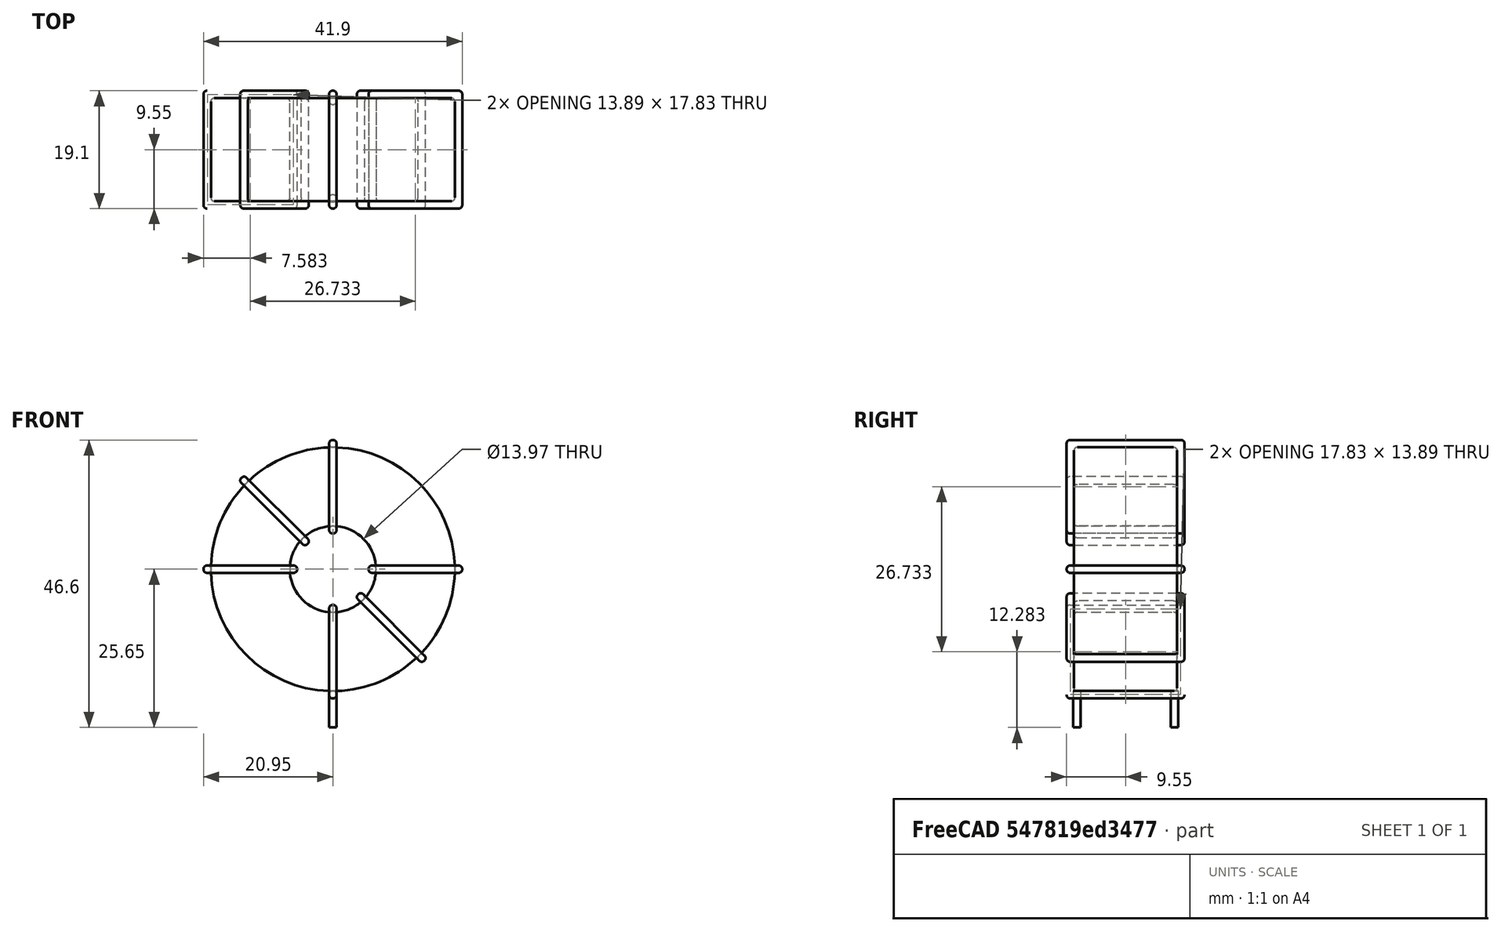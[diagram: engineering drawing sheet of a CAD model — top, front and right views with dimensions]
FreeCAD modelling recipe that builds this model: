
FCSTD DOCUMENT  (FreeCAD 0.16R6703 (Git))
Label: L_Toroid_Vertical_L41.9mm_W19.1mm_P15.80mm_Vishay_TJ7
License: All rights reserved
LicenseURL: http://en.wikipedia.org/wiki/All_rights_reserved
objects: Sketcher::SketchObject×6, PartDesign::Pad×6, PartDesign::Fillet×5, Spreadsheet::Sheet×1
note: 23 computed .brp shape members not serialized (recipe doc carries the construction recipe); baked Part::Feature solids carry a one-line shape summary decoded from their .brp

FEATURE [Spreadsheet::Sheet] Spreadsheet  label="dimensions"
  cells = A1=Wx; B1(Wx)=41.9; C1(WW)=13.96666666666667; D1=41.9; A2=Wy; B2(Wy)=19.1; D2=19.1; A3=RM; B3(RMx)=15.8; C3(RMy)=0; A4=d_wire; B4(d_wire)=1.2; A5=H; B5(H)=41.9; A6=offsetx; B6(offsetx)=20.95
FEATURE [Sketcher::SketchObject] Sketch
  Placement = pos=(0,-7.9,0) rot=(1,0,0;1.5708rad)
  expr: Placement.Base.y = -Spreadsheet.RMx / 2
  expr: Constraints[0] = Spreadsheet.Wx / 2 - Spreadsheet.d_wire
  expr: Constraints[4] = Spreadsheet.WW / 2
  expr: Constraints[2] = Spreadsheet.Wx / 2 + Spreadsheet.d_wire + 0.5
  sketch-geometry (2):
    g0: Circle CenterX=0 CenterY=22.65 CenterZ=0 NormalX=0 NormalY=0 NormalZ=1 Radius=19.75
    g1: Circle CenterX=0 CenterY=22.65 CenterZ=0 NormalX=0 NormalY=0 NormalZ=1 Radius=6.98333
  constraints (5):
    c: Radius(g0) = 19.75
    c: DistanceX(g-1,g0) = 0
    c: DistanceY(g-1,g0) = 22.65
    c: Coincident(g1,g0)
    c: Radius(g1) = 6.98333
FEATURE [PartDesign::Pad] Pad
  Length = 16.7
  Length2 = 100
  Midplane = true
  Placement = pos=(0,-7.9,0) rot=(1,0,0;1.5708rad)
  Sketch = -> Sketch
  Type = 0
  expr: Length = Spreadsheet.Wy - 2 * Spreadsheet.d_wire
FEATURE [Sketcher::SketchObject] Sketch001
  Placement = pos=(0,0,1.7) rot=(0,0,1;0rad)
  expr: Placement.Base.z = 0.5 + Spreadsheet.d_wire
  expr: Constraints[4] = Spreadsheet.RMy
  expr: Constraints[2] = -Spreadsheet.RMx
  expr: Constraints[1] = Spreadsheet.d_wire / 2
  sketch-geometry (2):
    g0: Circle CenterX=0 CenterY=0 CenterZ=0 NormalX=0 NormalY=0 NormalZ=1 Radius=0.6
    g1: Circle CenterX=0 CenterY=-15.8 CenterZ=0 NormalX=0 NormalY=0 NormalZ=1 Radius=0.6
  constraints (5):
    c: Equal(g0,g1)
    c: Radius(g0) = 0.6
    c: DistanceY(g-1,g1) = -15.8
    c: Coincident(g0,g-1)
    c: DistanceX(g-1,g1) = 0
FEATURE [PartDesign::Pad] Pad001
  Length = 1.2
  Length2 = 4.7
  Placement = pos=(0,0,1.7) rot=(0,0,1;0rad)
  Reversed = true
  Sketch = -> Sketch001
  Type = 4
  expr: Length2 = 3.5 + Spreadsheet.d_wire
  expr: Length = Spreadsheet.d_wire
FEATURE [PartDesign::Fillet] Fillet
  Base = -> Pad [Edge6,Edge3,Edge2]
  Placement = pos=(0,-7.9,0) rot=(1,0,0;1.5708rad)
  Radius = 0.5
FEATURE [Sketcher::SketchObject] Sketch003
  Placement = pos=(0,1.65,22.65) rot=(1,0,0;3.14159rad)
  expr: Constraints[18] = Spreadsheet.d_wire
  expr: Constraints[16] = Spreadsheet.d_wire
  expr: Constraints[19] = Spreadsheet.d_wire
  expr: Constraints[17] = Spreadsheet.d_wire
  expr: Placement.Base.y = -1 * (Spreadsheet.RMx - Spreadsheet.Wy) / 2
  expr: Constraints[21] = (Spreadsheet.Wx - Spreadsheet.WW) / 2 - Spreadsheet.d_wire
  expr: Constraints[22] = Spreadsheet.Wx / 2 - Spreadsheet.d_wire
  expr: Constraints[43] = Spreadsheet.d_wire
  expr: Constraints[48] = Spreadsheet.Wx - Spreadsheet.d_wire * 2
  expr: Constraints[49] = Spreadsheet.Wy
  expr: Placement.Base.z = Spreadsheet.Wx / 2 + Spreadsheet.d_wire + 0.5
  sketch-geometry (16):
    g0: LineSegment StartX=-5.78333 StartY=0 StartZ=0 EndX=-20.95 EndY=0 EndZ=0
    g1: LineSegment StartX=-20.95 StartY=0 StartZ=0 EndX=-20.95 EndY=19.1 EndZ=0
    g2: LineSegment StartX=-20.95 StartY=19.1 StartZ=0 EndX=-5.78333 EndY=19.1 EndZ=0
    g3: LineSegment StartX=-5.78333 StartY=19.1 StartZ=0 EndX=-5.78333 EndY=0 EndZ=0
    g4: LineSegment StartX=-19.75 StartY=17.9 StartZ=0 EndX=-6.98333 EndY=17.9 EndZ=0
    g5: LineSegment StartX=-6.98333 StartY=17.9 StartZ=0 EndX=-6.98333 EndY=1.2 EndZ=0
    g6: LineSegment StartX=-6.98333 StartY=1.2 StartZ=0 EndX=-19.75 EndY=1.2 EndZ=0
    g7: LineSegment StartX=-19.75 StartY=1.2 StartZ=0 EndX=-19.75 EndY=17.9 EndZ=0
    g8: LineSegment StartX=5.78333 StartY=19.1 StartZ=0 EndX=20.95 EndY=19.1 EndZ=0
    g9: LineSegment StartX=20.95 StartY=19.1 StartZ=0 EndX=20.95 EndY=0 EndZ=0
    g10: LineSegment StartX=20.95 StartY=0 StartZ=0 EndX=5.78333 EndY=0 EndZ=0
    g11: LineSegment StartX=5.78333 StartY=0 StartZ=0 EndX=5.78333 EndY=19.1 EndZ=0
    g12: LineSegment StartX=6.98333 StartY=17.9 StartZ=0 EndX=19.75 EndY=17.9 EndZ=0
    g13: LineSegment StartX=19.75 StartY=17.9 StartZ=0 EndX=19.75 EndY=1.2 EndZ=0
    g14: LineSegment StartX=19.75 StartY=1.2 StartZ=0 EndX=6.98333 EndY=1.2 EndZ=0
    g15: LineSegment StartX=6.98333 StartY=1.2 StartZ=0 EndX=6.98333 EndY=17.9 EndZ=0
  constraints (50):
    c: Horizontal(g0)
    c: Coincident(g1,g0)
    c: Vertical(g1)
    c: Coincident(g2,g1)
    c: Horizontal(g2)
    c: Coincident(g3,g2)
    c: Coincident(g3,g0)
    c: Vertical(g3)
    c: Coincident(g4,g5)
    c: Coincident(g5,g6)
    c: Coincident(g6,g7)
    c: Coincident(g7,g4)
    c: Horizontal(g4)
    c: Horizontal(g6)
    c: Vertical(g5)
    c: Vertical(g7)
    c: DistanceX(g1,g4) = 1.2
    c: DistanceY(g4,g1) = 1.2
    c: DistanceX(g5,g0) = 1.2
    c: DistanceY(g0,g5) = 1.2
    c: DistanceY(g-1,g0) = 0
    c: DistanceX(g6,g6) = 12.7667
    c: DistanceX(g6,g-1) = 19.75
    c: Coincident(g8,g9)
    c: Coincident(g9,g10)
    c: Coincident(g10,g11)
    c: Coincident(g11,g8)
    c: Horizontal(g8)
    c: Horizontal(g10)
    c: Vertical(g9)
    c: Vertical(g11)
    c: Coincident(g12,g13)
    c: Coincident(g13,g14)
    c: Coincident(g14,g15)
    c: Coincident(g15,g12)
    c: Horizontal(g12)
    c: Horizontal(g14)
    c: Vertical(g13)
    c: Vertical(g15)
    c: DistanceY(g8,g2) = 0
    c: DistanceY(g10,g0) = 0
    c: DistanceY(g14,g5) = 0
    c: DistanceY(g12,g4) = 0
    c: DistanceX(g8,g12) = 1.2
    c: Equal(g8,g2)
    c: Equal(g12,g4)
    c: Equal(g9,g1)
    c: Equal(g13,g7)
    c: DistanceX(g4,g12) = 39.5
    c: DistanceY(g0,g1) = 19.1
FEATURE [PartDesign::Pad] Pad002
  Length = 1.2
  Length2 = 100
  Midplane = true
  Placement = pos=(0,1.65,22.65) rot=(1,0,0;3.14159rad)
  Sketch = -> Sketch003
  Type = 0
  expr: Length = Spreadsheet.d_wire
FEATURE [PartDesign::Fillet] Fillet001
  Base = -> Pad002 [Edge38,Edge41,Edge42,Edge43,Edge29,Edge32,Edge33,Edge34,Edge25,Edge35,Edge36,Edge13,Edge14,Edge15,Edge16,Edge17,Edge18,Edge19,Edge1,Edge2,Edge3,Edge4,Edge5,Edge6,Edge7,Edge37,Edge39,Edge40,Edge20,Edge23,Edge24,Edge21,Edge22,Edge8,Edge9,Edge10,Edge11,Edge12,Edge26,Edge27,+8 more]
  Placement = pos=(0,1.65,22.65) rot=(1,0,0;3.14159rad)
  Radius = 0.564
  expr: Radius = Spreadsheet.d_wire * 0.47
FEATURE [Sketcher::SketchObject] Sketch004
  Placement = pos=(0,1.65,22.65) rot=(0.92388,0,0.382683;3.14159rad)
  expr: Constraints[18] = Spreadsheet.d_wire
  expr: Constraints[16] = Spreadsheet.d_wire
  expr: Constraints[19] = Spreadsheet.d_wire
  expr: Constraints[17] = Spreadsheet.d_wire
  expr: Placement.Base.y = -1 * (Spreadsheet.RMx - Spreadsheet.Wy) / 2
  expr: Constraints[21] = (Spreadsheet.Wx - Spreadsheet.WW) / 2 - Spreadsheet.d_wire
  expr: Constraints[22] = Spreadsheet.Wx / 2 - Spreadsheet.d_wire
  expr: Constraints[43] = Spreadsheet.d_wire
  expr: Constraints[48] = Spreadsheet.Wx - 2 * Spreadsheet.d_wire
  expr: Constraints[49] = Spreadsheet.Wy
  expr: Placement.Base.z = Spreadsheet.Wx / 2 + Spreadsheet.d_wire + 0.5
  sketch-geometry (16):
    g0: LineSegment StartX=-5.78333 StartY=0 StartZ=0 EndX=-20.95 EndY=0 EndZ=0
    g1: LineSegment StartX=-20.95 StartY=0 StartZ=0 EndX=-20.95 EndY=19.1 EndZ=0
    g2: LineSegment StartX=-20.95 StartY=19.1 StartZ=0 EndX=-5.78333 EndY=19.1 EndZ=0
    g3: LineSegment StartX=-5.78333 StartY=19.1 StartZ=0 EndX=-5.78333 EndY=0 EndZ=0
    g4: LineSegment StartX=-19.75 StartY=17.9 StartZ=0 EndX=-6.98333 EndY=17.9 EndZ=0
    g5: LineSegment StartX=-6.98333 StartY=17.9 StartZ=0 EndX=-6.98333 EndY=1.2 EndZ=0
    g6: LineSegment StartX=-6.98333 StartY=1.2 StartZ=0 EndX=-19.75 EndY=1.2 EndZ=0
    g7: LineSegment StartX=-19.75 StartY=1.2 StartZ=0 EndX=-19.75 EndY=17.9 EndZ=0
    g8: LineSegment StartX=5.78333 StartY=19.1 StartZ=0 EndX=20.95 EndY=19.1 EndZ=0
    g9: LineSegment StartX=20.95 StartY=19.1 StartZ=0 EndX=20.95 EndY=0 EndZ=0
    g10: LineSegment StartX=20.95 StartY=0 StartZ=0 EndX=5.78333 EndY=0 EndZ=0
    g11: LineSegment StartX=5.78333 StartY=0 StartZ=0 EndX=5.78333 EndY=19.1 EndZ=0
    g12: LineSegment StartX=6.98333 StartY=17.9 StartZ=0 EndX=19.75 EndY=17.9 EndZ=0
    g13: LineSegment StartX=19.75 StartY=17.9 StartZ=0 EndX=19.75 EndY=1.2 EndZ=0
    g14: LineSegment StartX=19.75 StartY=1.2 StartZ=0 EndX=6.98333 EndY=1.2 EndZ=0
    g15: LineSegment StartX=6.98333 StartY=1.2 StartZ=0 EndX=6.98333 EndY=17.9 EndZ=0
  constraints (50):
    c: Horizontal(g0)
    c: Coincident(g1,g0)
    c: Vertical(g1)
    c: Coincident(g2,g1)
    c: Horizontal(g2)
    c: Coincident(g3,g2)
    c: Coincident(g3,g0)
    c: Vertical(g3)
    c: Coincident(g4,g5)
    c: Coincident(g5,g6)
    c: Coincident(g6,g7)
    c: Coincident(g7,g4)
    c: Horizontal(g4)
    c: Horizontal(g6)
    c: Vertical(g5)
    c: Vertical(g7)
    c: DistanceX(g1,g4) = 1.2
    c: DistanceY(g4,g1) = 1.2
    c: DistanceX(g5,g0) = 1.2
    c: DistanceY(g0,g5) = 1.2
    c: DistanceY(g-1,g0) = 0
    c: DistanceX(g6,g6) = 12.7667
    c: DistanceX(g6,g-1) = 19.75
    c: Coincident(g8,g9)
    c: Coincident(g9,g10)
    c: Coincident(g10,g11)
    c: Coincident(g11,g8)
    c: Horizontal(g8)
    c: Horizontal(g10)
    c: Vertical(g9)
    c: Vertical(g11)
    c: Coincident(g12,g13)
    c: Coincident(g13,g14)
    c: Coincident(g14,g15)
    c: Coincident(g15,g12)
    c: Horizontal(g12)
    c: Horizontal(g14)
    c: Vertical(g13)
    c: Vertical(g15)
    c: DistanceY(g8,g2) = 0
    c: DistanceY(g10,g0) = 0
    c: DistanceY(g14,g5) = 0
    c: DistanceY(g12,g4) = 0
    c: DistanceX(g8,g12) = 1.2
    c: Equal(g8,g2)
    c: Equal(g12,g4)
    c: Equal(g9,g1)
    c: Equal(g13,g7)
    c: DistanceX(g4,g12) = 39.5
    c: DistanceY(g0,g1) = 19.1
FEATURE [PartDesign::Pad] Pad003
  Length = 1.2
  Length2 = 100
  Midplane = true
  Placement = pos=(0,1.65,22.65) rot=(0.92388,0,0.382683;3.14159rad)
  Sketch = -> Sketch004
  Type = 0
  expr: Length = Spreadsheet.d_wire
FEATURE [PartDesign::Fillet] Fillet002
  Base = -> Pad003 [Edge38,Edge41,Edge42,Edge43,Edge29,Edge32,Edge33,Edge34,Edge25,Edge35,Edge36,Edge13,Edge14,Edge15,Edge16,Edge17,Edge18,Edge19,Edge1,Edge2,Edge3,Edge4,Edge5,Edge6,Edge7,Edge37,Edge39,Edge40,Edge20,Edge23,Edge24,Edge21,Edge22,Edge8,Edge9,Edge10,Edge11,Edge12,Edge26,Edge27,+8 more]
  Placement = pos=(0,1.65,22.65) rot=(0.92388,0,0.382683;3.14159rad)
  Radius = 0.564
  expr: Radius = Spreadsheet.d_wire * 0.47
FEATURE [Sketcher::SketchObject] Sketch005
  Placement = pos=(0,1.65,22.65) rot=(0.92388,0,-0.382683;3.14159rad)
  expr: Constraints[18] = Spreadsheet.d_wire
  expr: Constraints[16] = Spreadsheet.d_wire
  expr: Constraints[19] = Spreadsheet.d_wire
  expr: Constraints[17] = Spreadsheet.d_wire
  expr: Placement.Base.y = -1 * (Spreadsheet.RMx - Spreadsheet.Wy) / 2
  expr: Constraints[21] = (Spreadsheet.Wx - Spreadsheet.WW) / 2 - Spreadsheet.d_wire
  expr: Constraints[22] = Spreadsheet.Wx / 2 - Spreadsheet.d_wire
  expr: Constraints[43] = Spreadsheet.d_wire
  expr: Constraints[48] = Spreadsheet.Wx - 2 * Spreadsheet.d_wire
  expr: Constraints[49] = Spreadsheet.Wy
  expr: Placement.Base.z = Spreadsheet.Wx / 2 + Spreadsheet.d_wire + 0.5
  sketch-geometry (16):
    g0: LineSegment StartX=-5.78333 StartY=0 StartZ=0 EndX=-20.95 EndY=0 EndZ=0
    g1: LineSegment StartX=-20.95 StartY=0 StartZ=0 EndX=-20.95 EndY=19.1 EndZ=0
    g2: LineSegment StartX=-20.95 StartY=19.1 StartZ=0 EndX=-5.78333 EndY=19.1 EndZ=0
    g3: LineSegment StartX=-5.78333 StartY=19.1 StartZ=0 EndX=-5.78333 EndY=0 EndZ=0
    g4: LineSegment StartX=-19.75 StartY=17.9 StartZ=0 EndX=-6.98333 EndY=17.9 EndZ=0
    g5: LineSegment StartX=-6.98333 StartY=17.9 StartZ=0 EndX=-6.98333 EndY=1.2 EndZ=0
    g6: LineSegment StartX=-6.98333 StartY=1.2 StartZ=0 EndX=-19.75 EndY=1.2 EndZ=0
    g7: LineSegment StartX=-19.75 StartY=1.2 StartZ=0 EndX=-19.75 EndY=17.9 EndZ=0
    g8: LineSegment StartX=5.78333 StartY=19.1 StartZ=0 EndX=20.95 EndY=19.1 EndZ=0
    g9: LineSegment StartX=20.95 StartY=19.1 StartZ=0 EndX=20.95 EndY=0 EndZ=0
    g10: LineSegment StartX=20.95 StartY=0 StartZ=0 EndX=5.78333 EndY=0 EndZ=0
    g11: LineSegment StartX=5.78333 StartY=0 StartZ=0 EndX=5.78333 EndY=19.1 EndZ=0
    g12: LineSegment StartX=6.98333 StartY=17.9 StartZ=0 EndX=19.75 EndY=17.9 EndZ=0
    g13: LineSegment StartX=19.75 StartY=17.9 StartZ=0 EndX=19.75 EndY=1.2 EndZ=0
    g14: LineSegment StartX=19.75 StartY=1.2 StartZ=0 EndX=6.98333 EndY=1.2 EndZ=0
    g15: LineSegment StartX=6.98333 StartY=1.2 StartZ=0 EndX=6.98333 EndY=17.9 EndZ=0
  constraints (50):
    c: Horizontal(g0)
    c: Coincident(g1,g0)
    c: Vertical(g1)
    c: Coincident(g2,g1)
    c: Horizontal(g2)
    c: Coincident(g3,g2)
    c: Coincident(g3,g0)
    c: Vertical(g3)
    c: Coincident(g4,g5)
    c: Coincident(g5,g6)
    c: Coincident(g6,g7)
    c: Coincident(g7,g4)
    c: Horizontal(g4)
    c: Horizontal(g6)
    c: Vertical(g5)
    c: Vertical(g7)
    c: DistanceX(g1,g4) = 1.2
    c: DistanceY(g4,g1) = 1.2
    c: DistanceX(g5,g0) = 1.2
    c: DistanceY(g0,g5) = 1.2
    c: DistanceY(g-1,g0) = 0
    c: DistanceX(g6,g6) = 12.7667
    c: DistanceX(g6,g-1) = 19.75
    c: Coincident(g8,g9)
    c: Coincident(g9,g10)
    c: Coincident(g10,g11)
    c: Coincident(g11,g8)
    c: Horizontal(g8)
    c: Horizontal(g10)
    c: Vertical(g9)
    c: Vertical(g11)
    c: Coincident(g12,g13)
    c: Coincident(g13,g14)
    c: Coincident(g14,g15)
    c: Coincident(g15,g12)
    c: Horizontal(g12)
    c: Horizontal(g14)
    c: Vertical(g13)
    c: Vertical(g15)
    c: DistanceY(g8,g2) = 0
    c: DistanceY(g10,g0) = 0
    c: DistanceY(g14,g5) = 0
    c: DistanceY(g12,g4) = 0
    c: DistanceX(g8,g12) = 1.2
    c: Equal(g8,g2)
    c: Equal(g12,g4)
    c: Equal(g9,g1)
    c: Equal(g13,g7)
    c: DistanceX(g4,g12) = 39.5
    c: DistanceY(g0,g1) = 19.1
FEATURE [PartDesign::Pad] Pad004
  Length = 1.2
  Length2 = 100
  Midplane = true
  Placement = pos=(0,1.65,22.65) rot=(0.92388,0,-0.382683;3.14159rad)
  Sketch = -> Sketch005
  Type = 0
  expr: Length = Spreadsheet.d_wire
FEATURE [PartDesign::Fillet] Fillet003
  Base = -> Pad004 [Edge38,Edge41,Edge42,Edge43,Edge29,Edge32,Edge33,Edge34,Edge25,Edge35,Edge36,Edge13,Edge14,Edge15,Edge16,Edge17,Edge18,Edge19,Edge1,Edge2,Edge3,Edge4,Edge5,Edge6,Edge7,Edge37,Edge39,Edge40,Edge20,Edge23,Edge24,Edge21,Edge22,Edge8,Edge9,Edge10,Edge11,Edge12,Edge26,Edge27,+8 more]
  Placement = pos=(0,1.65,22.65) rot=(0.92388,0,-0.382683;3.14159rad)
  Radius = 0.564
  expr: Radius = Spreadsheet.d_wire * 0.47
FEATURE [Sketcher::SketchObject] Sketch006
  Placement = pos=(0,1.65,22.65) rot=(0.707107,0,0.707107;3.14159rad)
  expr: Constraints[18] = Spreadsheet.d_wire
  expr: Constraints[16] = Spreadsheet.d_wire
  expr: Constraints[19] = Spreadsheet.d_wire
  expr: Constraints[17] = Spreadsheet.d_wire
  expr: Placement.Base.y = -1 * (Spreadsheet.RMx - Spreadsheet.Wy) / 2
  expr: Constraints[21] = (Spreadsheet.Wx - Spreadsheet.WW) / 2 - Spreadsheet.d_wire
  expr: Constraints[22] = Spreadsheet.Wx / 2 - Spreadsheet.d_wire
  expr: Constraints[43] = Spreadsheet.d_wire
  expr: Constraints[48] = Spreadsheet.Wx - Spreadsheet.d_wire * 2
  expr: Constraints[49] = Spreadsheet.Wy
  expr: Placement.Base.z = Spreadsheet.Wx / 2 + Spreadsheet.d_wire + 0.5
  sketch-geometry (16):
    g0: LineSegment StartX=-5.78333 StartY=0 StartZ=0 EndX=-20.95 EndY=0 EndZ=0
    g1: LineSegment StartX=-20.95 StartY=0 StartZ=0 EndX=-20.95 EndY=19.1 EndZ=0
    g2: LineSegment StartX=-20.95 StartY=19.1 StartZ=0 EndX=-5.78333 EndY=19.1 EndZ=0
    g3: LineSegment StartX=-5.78333 StartY=19.1 StartZ=0 EndX=-5.78333 EndY=0 EndZ=0
    g4: LineSegment StartX=-19.75 StartY=17.9 StartZ=0 EndX=-6.98333 EndY=17.9 EndZ=0
    g5: LineSegment StartX=-6.98333 StartY=17.9 StartZ=0 EndX=-6.98333 EndY=1.2 EndZ=0
    g6: LineSegment StartX=-6.98333 StartY=1.2 StartZ=0 EndX=-19.75 EndY=1.2 EndZ=0
    g7: LineSegment StartX=-19.75 StartY=1.2 StartZ=0 EndX=-19.75 EndY=17.9 EndZ=0
    g8: LineSegment StartX=5.78333 StartY=19.1 StartZ=0 EndX=20.95 EndY=19.1 EndZ=0
    g9: LineSegment StartX=20.95 StartY=19.1 StartZ=0 EndX=20.95 EndY=0 EndZ=0
    g10: LineSegment StartX=20.95 StartY=0 StartZ=0 EndX=5.78333 EndY=0 EndZ=0
    g11: LineSegment StartX=5.78333 StartY=0 StartZ=0 EndX=5.78333 EndY=19.1 EndZ=0
    g12: LineSegment StartX=6.98333 StartY=17.9 StartZ=0 EndX=19.75 EndY=17.9 EndZ=0
    g13: LineSegment StartX=19.75 StartY=17.9 StartZ=0 EndX=19.75 EndY=1.2 EndZ=0
    g14: LineSegment StartX=19.75 StartY=1.2 StartZ=0 EndX=6.98333 EndY=1.2 EndZ=0
    g15: LineSegment StartX=6.98333 StartY=1.2 StartZ=0 EndX=6.98333 EndY=17.9 EndZ=0
  constraints (50):
    c: Horizontal(g0)
    c: Coincident(g1,g0)
    c: Vertical(g1)
    c: Coincident(g2,g1)
    c: Horizontal(g2)
    c: Coincident(g3,g2)
    c: Coincident(g3,g0)
    c: Vertical(g3)
    c: Coincident(g4,g5)
    c: Coincident(g5,g6)
    c: Coincident(g6,g7)
    c: Coincident(g7,g4)
    c: Horizontal(g4)
    c: Horizontal(g6)
    c: Vertical(g5)
    c: Vertical(g7)
    c: DistanceX(g1,g4) = 1.2
    c: DistanceY(g4,g1) = 1.2
    c: DistanceX(g5,g0) = 1.2
    c: DistanceY(g0,g5) = 1.2
    c: DistanceY(g-1,g0) = 0
    c: DistanceX(g6,g6) = 12.7667
    c: DistanceX(g6,g-1) = 19.75
    c: Coincident(g8,g9)
    c: Coincident(g9,g10)
    c: Coincident(g10,g11)
    c: Coincident(g11,g8)
    c: Horizontal(g8)
    c: Horizontal(g10)
    c: Vertical(g9)
    c: Vertical(g11)
    c: Coincident(g12,g13)
    c: Coincident(g13,g14)
    c: Coincident(g14,g15)
    c: Coincident(g15,g12)
    c: Horizontal(g12)
    c: Horizontal(g14)
    c: Vertical(g13)
    c: Vertical(g15)
    c: DistanceY(g8,g2) = 0
    c: DistanceY(g10,g0) = 0
    c: DistanceY(g14,g5) = 0
    c: DistanceY(g12,g4) = 0
    c: DistanceX(g8,g12) = 1.2
    c: Equal(g8,g2)
    c: Equal(g12,g4)
    c: Equal(g9,g1)
    c: Equal(g13,g7)
    c: DistanceX(g4,g12) = 39.5
    c: DistanceY(g0,g1) = 19.1
FEATURE [PartDesign::Pad] Pad005
  Length = 1.2
  Length2 = 100
  Midplane = true
  Placement = pos=(0,1.65,22.65) rot=(0.707107,0,0.707107;3.14159rad)
  Sketch = -> Sketch006
  Type = 0
  expr: Length = Spreadsheet.d_wire
FEATURE [PartDesign::Fillet] Fillet004
  Base = -> Pad005 [Edge38,Edge41,Edge42,Edge43,Edge29,Edge32,Edge33,Edge34,Edge25,Edge35,Edge36,Edge13,Edge14,Edge15,Edge16,Edge17,Edge18,Edge19,Edge1,Edge2,Edge3,Edge4,Edge5,Edge6,Edge7,Edge37,Edge39,Edge40,Edge20,Edge23,Edge24,Edge21,Edge22,Edge8,Edge9,Edge10,Edge11,Edge12,Edge26,Edge27,+8 more]
  Placement = pos=(0,1.65,22.65) rot=(0.707107,0,0.707107;3.14159rad)
  Radius = 0.564
  expr: Radius = Spreadsheet.d_wire * 0.47
